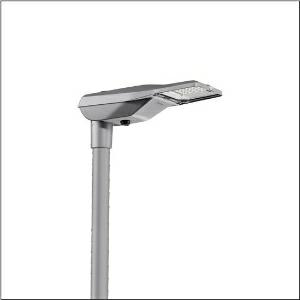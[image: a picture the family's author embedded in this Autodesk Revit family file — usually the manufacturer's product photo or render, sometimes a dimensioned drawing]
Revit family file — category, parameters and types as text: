
# Revit family: streetlight_sl_21_iq_micro___p0_8ab_5xe1r31u08db_7cfa
name_source: partatom
category: Lighting Fixtures
units: mm (PartAtom-declared; Revit-internal decimal feet)

## family parameters
Cut with Voids When Loaded = No
Host = Face
Light Source = No
Part Type = Normal
Room Calculation Point = No
Round Connector Dimension = Use Diameter
Shared = No

## types (1)
- --- (1 x LED, 4550 lm, 39.1 W, 3000K)
    Apparent Load = 39 VA
    CIE Flux Codes = 36 71 98 100 100
    Color Rendering = 70
    Color Temperature = 3000K
    Default Elevation = 1800 mm
    Description = Streetlight SL 21 iQ micro, mast luminaire, primary light control with lens, of PMMA, primary optical cover: cover, of toughened safety glass, transparent, light distribution: P0.8aB, light emission: direct distribution, primary light characteristic: asymmetric, installation type: post-top, side-entry, LED, High Power LED, rated luminous flux: 4.550lm, luminous efficacy: 116lm/W, light colour: 730, colour temperature: 3000K, control gear: iQ-Street Remote, D4i with power reduction, control: pre-setting: logarithmic dimming characteristic, Street-Remote, Auto-Match, Temp-Guard, Lumen-Switch, Night-Set, Smart-Wire, Light-Fading, Desk-Remote (wireless, voltage-free reading and setting of iQ features in the workshop via application-optimized NFC function/RFID function), optimised constant luminous flux control (CLO 2.0), mains connection: 220..240V, AC, 50/60Hz, start of lifetime: 39W, end of service life: 41W, reduction: 17W, luminaire housing, of diecast aluminium, powder-coated, Siteco® metallic grey (DB 702S), corrosivity category C5 mid according to DIN EN ISO 12944, please order mast flange separately, inclination adjustable: 0°, 5°, 10°, 15°, sealing non-destructively replaceable, multi-level sealing system, length: 528mm, width: 235mm, height: 110mm, mast flange for spigot size: 42mm (side-entry): 5XC10008XM4, 60/48mm (side-entry/post-top): 5XC10108XM2, 76/60mm (side-entry/post-top): 5XC10108XM1, mounting height: 4..8m, Smart Interface below, protection rating (complete): IP66, insulation class (complete): insulation class II (safety insulation), certification: CE, ENEC, ENEC+, VDE, impact resistance: IK10, permissible operating ambient temperature for outdoor applications: -40..+50°C, standard-compliant lighting for roads and squares, packaging unit: 1 piece

Light Distribution: P0.8aB
    Height = 110 mm
    Lamp = 1 x LED
    Lamp Light Flux = 4550 lm
    Lamp Power = 39.1 W
    Lamp count = 1
    Length = 528 mm
    Luminous efficacy = 116 lm/W
    Manufacturer = Siteco
    ModVariant = No
    Model = 5XE1R31U08DB
    Number of Poles = 1
    OnlyDefault = Yes
    Power Factor = 1
    Product Name = Streetlight SL 21 iQ micro | P0.8aB
    Product group = mast luminaire | pylon top
    ProductGroupID = 6100
    Protection Class = Protection class II
    Protection Degree = IP 66
    RLX_Detail_Level = 1
    RLX_Emergency_Light_Flux = 0 lm
    RLX_Emergency_Type = 0
    RLX_Emergency_Type_DB = No
    RlxData = <blob elided: 99085 chars, md5=109e6a99>
    Socket = socket
    Standby Power = 0 W
    System Light Flux = 4550 lm
    System Power = 39 W
    Type Comments = factory setting: luminous flux: 100 % | dim-lin: 254 | 765 mA
    Type Image = l_1277290.jpg
    URL = http://relux.com
    VarID = @adj_097219
    Voltage = 0 V
    Weight = 0.00 kg
    Width = 235 mm

## geometry (parser evidence)
native form markers: Blend x4, Sweep x10
no freeform markers — native parametric forms only
